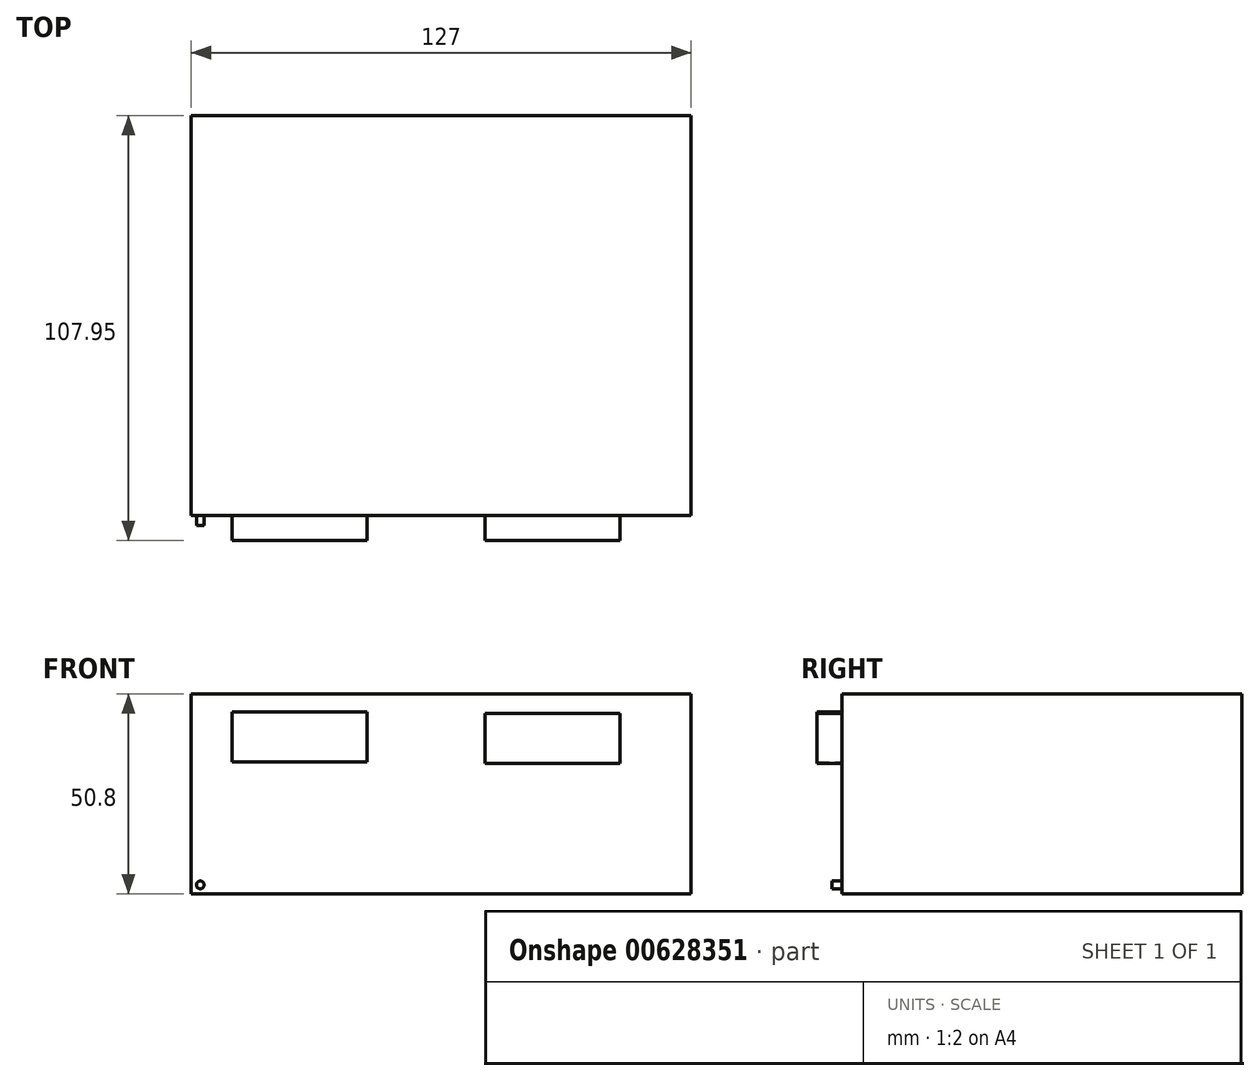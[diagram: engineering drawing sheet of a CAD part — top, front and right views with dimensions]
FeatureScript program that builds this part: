
annotation { "Feature Type Name" : "Feature", "Feature Type Description" : "" }
export const myFeature = defineFeature(function(context is Context, id is Id, definition is map)
    precondition{}
    {
        {
            var Q0;
            Q0=qCreatedBy(makeId("Top.planeOp"),FACE);
            var sketch = newSketch(context, id + "F0", { "sketchPlane" : qUnion([Q0])});
            skLineSegment(sketch, "E0.bottom", {"start": v(-58.73, 43.26) * mm, "end": v(68.27, 43.26) * mm});
            skLineSegment(sketch, "E0.top", {"start": v(-58.73, -58.34) * mm, "end": v(68.27, -58.34) * mm});
            skLineSegment(sketch, "E0.left", {"start": v(-58.73, 43.26) * mm, "end": v(-58.73, -58.34) * mm});
            skLineSegment(sketch, "E0.right", {"start": v(68.27, 43.26) * mm, "end": v(68.27, -58.34) * mm});
            skSolve(sketch);
        }
        {
            var Q0;
            Q0 = qSketchRegion(id + "F0", true);
            extrude(context, id + "F1", {"entities" : qUnion([Q0]), "depth" : 50.8 * mm, "offsetDistance" : 25.4 * mm});
        }
        {
            var Q0;
            Q0=makeQuery(id+"F1.opExtrude","SWEPT_FACE",FACE,{"disambiguationData":[OSD([sQuery(id+"F0.wireOp",EDGE,"E0.top")])]});
            var sketch = newSketch(context, id + "F2", { "sketchPlane" : qUnion([Q0])});
            skCircle(sketch, "E1", {"center": v(-56.46, 2.29) * mm, "radius": 0.98 * mm});
            skSolve(sketch);
        }
        {
            var Q0;
            Q0 = qSketchRegion(id + "F2", true);
            extrude(context, id + "F3", {"entities" : qUnion([Q0]), "operationType" : NewBodyOperationType.ADD, "depth" : 2.54 * mm, "offsetDistance" : 25.4 * mm});
        }
        {
            var Q0;
            Q0=makeQuery(id+"F1.opExtrude","SWEPT_FACE",FACE,{"disambiguationData":[OSD([sQuery(id+"F0.wireOp",EDGE,"E0.top")])]});
            var sketch = newSketch(context, id + "F4", { "sketchPlane" : qUnion([Q0])});
            skLineSegment(sketch, "E2.bottom", {"start": v(-48.36, 46.19) * mm, "end": v(-14.07, 46.19) * mm});
            skLineSegment(sketch, "E2.top", {"start": v(-48.36, 33.49) * mm, "end": v(-14.07, 33.49) * mm});
            skLineSegment(sketch, "E2.left", {"start": v(-48.36, 46.19) * mm, "end": v(-48.36, 33.49) * mm});
            skLineSegment(sketch, "E2.right", {"start": v(-14.07, 46.19) * mm, "end": v(-14.07, 33.49) * mm});
            skSolve(sketch);
        }
        {
            var Q0;
            Q0 = qSketchRegion(id + "F4", true);
            var Q1;
            Q1=makeQuery(id+"F4.imprint","IMPRINT",FACE,{"disambiguationData":[TD([[makeQuery(id+"F4.imprint","IMPRINT",EDGE,{"derivedFrom":sQuery(id+"F4.wireOp",EDGE,"E2.bottom")}),-1.0]])]});
            extrude(context, id + "F5", {"entities" : qUnion([Q0, Q1]), "operationType" : NewBodyOperationType.ADD, "depth" : 6.35 * mm, "offsetDistance" : 25.4 * mm});
        }
        {
            var Q0;
            Q0=makeQuery(id+"F4.imprint","IMPRINT",FACE,{"disambiguationData":[TD([[makeQuery(id+"F4.imprint","IMPRINT",EDGE,{"derivedFrom":sQuery(id+"F4.wireOp",EDGE,"E2.bottom")}),1.0]])]});
            var sketch = newSketch(context, id + "F6", { "sketchPlane" : qUnion([Q0])});
            skLineSegment(sketch, "E3.bottom", {"start": v(15.9, 45.9) * mm, "end": v(50.18, 45.9) * mm});
            skLineSegment(sketch, "E3.top", {"start": v(15.9, 33.2) * mm, "end": v(50.18, 33.2) * mm});
            skLineSegment(sketch, "E3.left", {"start": v(15.9, 45.9) * mm, "end": v(15.9, 33.2) * mm});
            skLineSegment(sketch, "E3.right", {"start": v(50.18, 45.9) * mm, "end": v(50.18, 33.2) * mm});
            skSolve(sketch);
        }
        {
            var Q0;
            Q0 = qSketchRegion(id + "F6", true);
            extrude(context, id + "F7", {"entities" : qUnion([Q0]), "operationType" : NewBodyOperationType.ADD, "depth" : 6.35 * mm, "offsetDistance" : 25.4 * mm});
        }
    });
